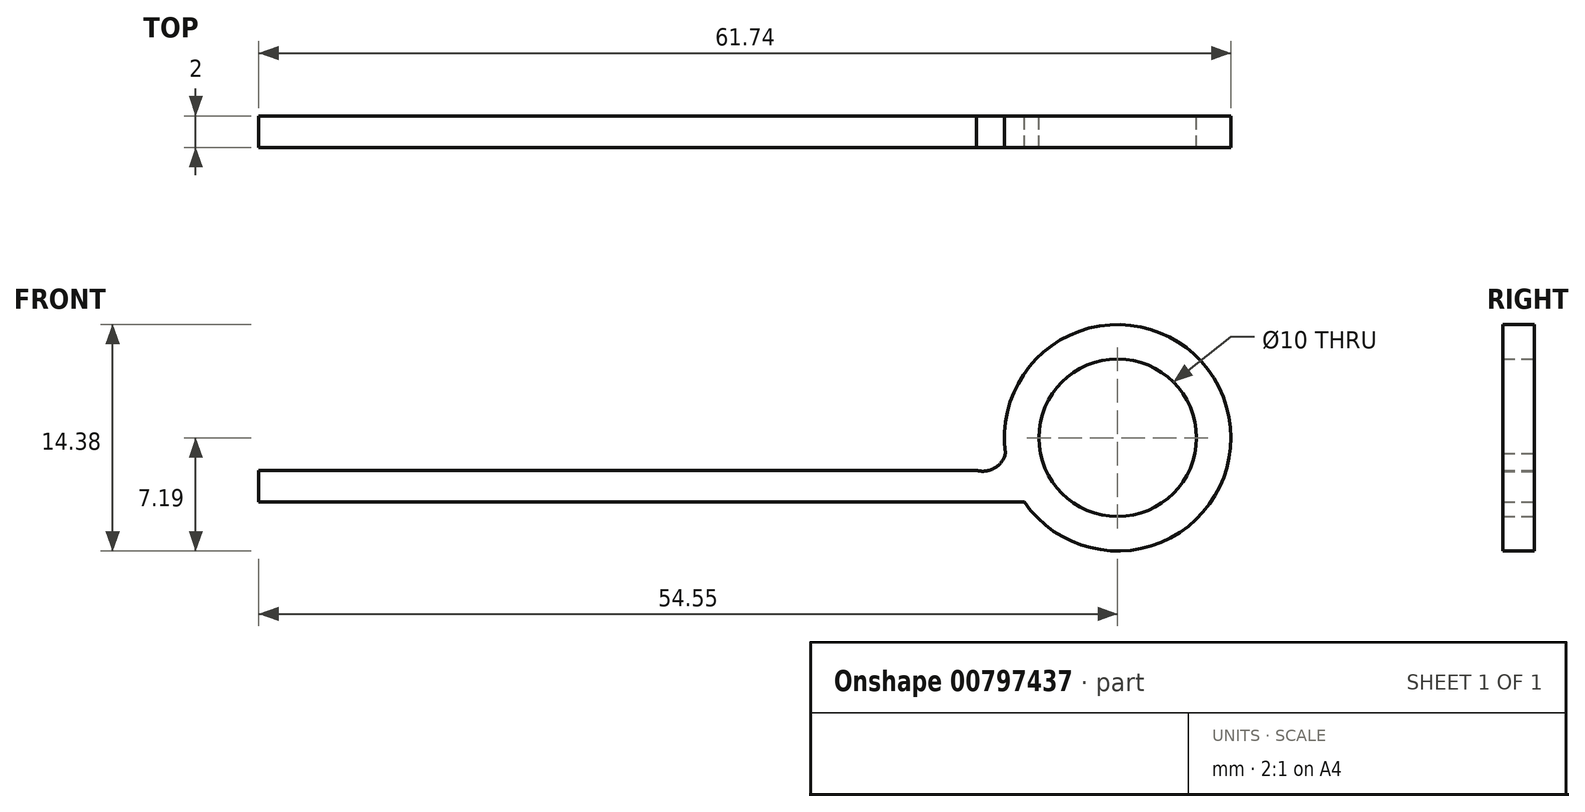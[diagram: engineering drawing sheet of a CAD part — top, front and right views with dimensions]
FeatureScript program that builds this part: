
annotation { "Feature Type Name" : "Feature", "Feature Type Description" : "" }
export const myFeature = defineFeature(function(context is Context, id is Id, definition is map)
    precondition{}
    {
        {
            var Q0;
            Q0=qCreatedBy(makeId("Front.planeOp"),FACE);
            var sketch = newSketch(context, id + "F0", { "sketchPlane" : qUnion([Q0])});
            skCircle(sketch, "E0", {"center": v(0, 0) * mm, "radius": 5 * mm});
            skArc(sketch, "E1", {"start": v(-5.93, -4.07) * mm, "mid": v(6.7, 2.6) * mm, "end": v(-7.12, -1) * mm});
            skLineSegment(sketch, "E2", {"start": v(-54.55, -2.07) * mm, "end": v(-54.55, -4.07) * mm});
            skLineSegment(sketch, "E3", {"start": v(-54.55, -4.07) * mm, "end": v(-5.93, -4.07) * mm});
            skArc(sketch, "E4", {"start": v(-5.93, -4.07) * mm, "mid": v(-4.72, -3.43) * mm, "end": v(-4.55, -2.07) * mm});
            skArc(sketch, "E5", {"start": v(-8.98, -2.07) * mm, "mid": v(-7.82, -1.93) * mm, "end": v(-7.12, -1) * mm});
            skLineSegment(sketch, "E6.trimOffspring", {"start": v(-8.14, -2.07) * mm, "end": v(-54.55, -2.07) * mm});
            skSolve(sketch);
        }
        {
            var Q0;
            Q0=makeQuery(id+"F0.imprint","IMPRINT",FACE,{"disambiguationData":[TD([[makeQuery(id+"F0.imprint","IMPRINT",EDGE,{"derivedFrom":sQuery(id+"F0.wireOp",EDGE,"E0")}),-1.0]])]});
            extrude(context, id + "F1", {"entities" : qUnion([Q0]), "depth" : 2 * mm, "offsetDistance" : 25 * mm});
        }
    });
